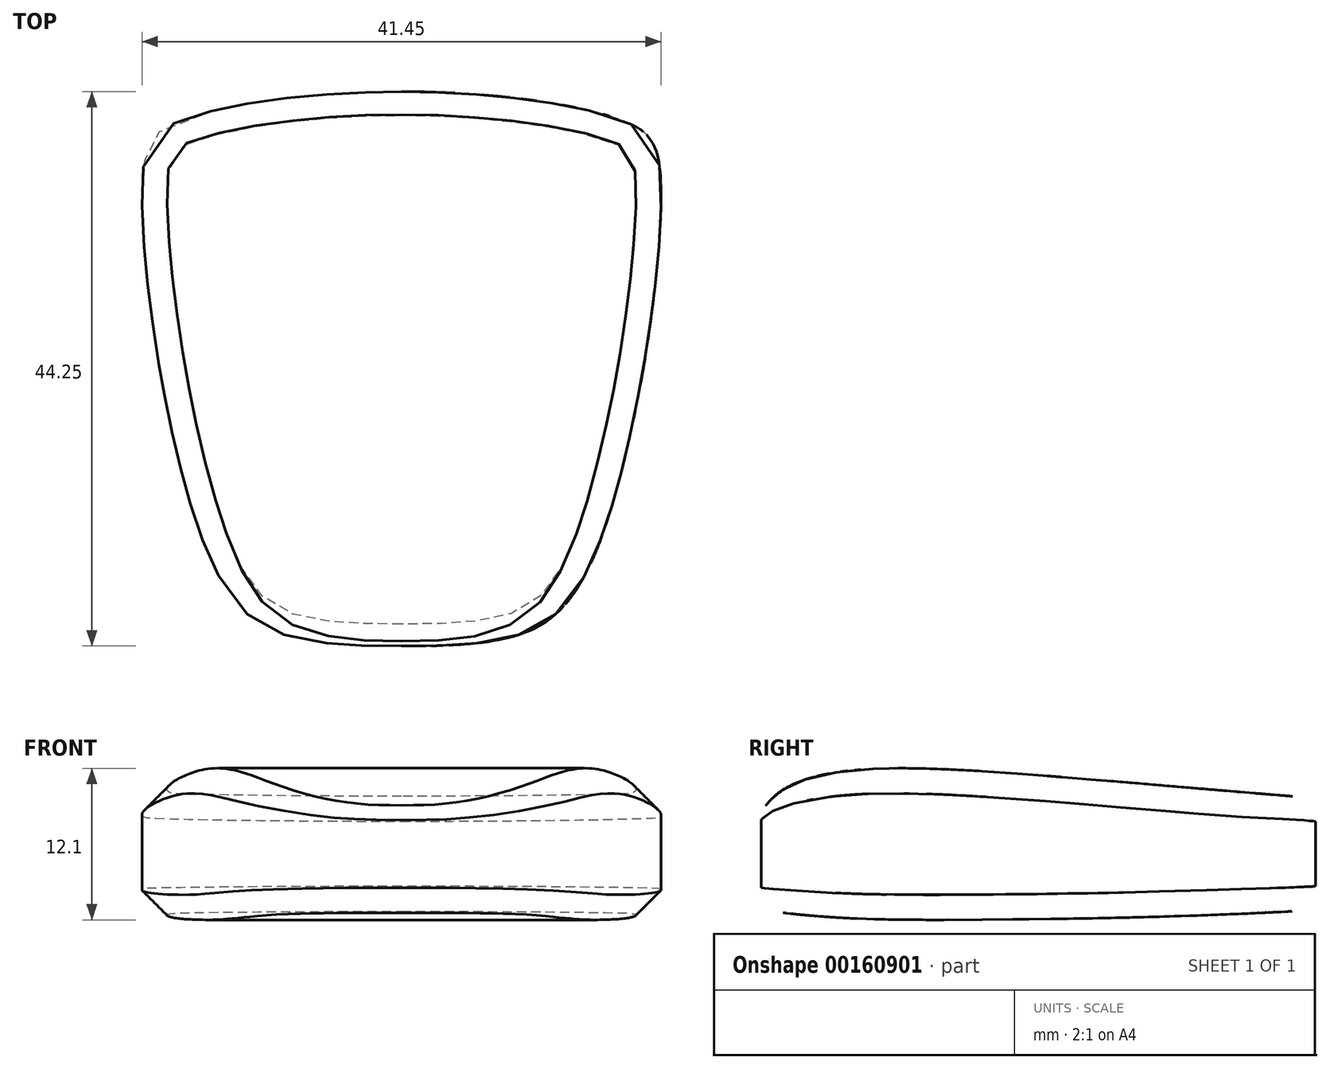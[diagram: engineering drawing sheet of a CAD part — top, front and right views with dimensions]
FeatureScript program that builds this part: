
annotation { "Feature Type Name" : "Feature", "Feature Type Description" : "" }
export const myFeature = defineFeature(function(context is Context, id is Id, definition is map)
    precondition{}
    {
        {
            var Q0;
            Q0=qCreatedBy(makeId("Top.planeOp"),FACE);
            var sketch = newSketch(context, id + "F0", { "sketchPlane" : qUnion([Q0])});
            skFitSpline(sketch, "E0", {"points": [v(0, 6.83) * mm, v(-18.05, 4.35) * mm, v(-20.68, 0) * mm, v(-15.04, -30.98) * mm, v(-8.66, -36.72) * mm, v(0, -37.42) * mm], "startDerivative": vector(-88.66, 0) * mm, "endDerivative": vector(58.86, 0) * mm});
            skFitSpline(sketch, "E1.MirrorCS", {"points": [v(0, 6.83) * mm, v(18.05, 4.35) * mm, v(20.68, 0) * mm, v(15.04, -30.98) * mm, v(8.66, -36.72) * mm, v(0, -37.42) * mm], "startDerivative": vector(88.66, 0) * mm, "endDerivative": vector(-58.86, 0) * mm});
            skSolve(sketch);
        }
        {
            var Q0;
            Q0 = qSketchRegion(id + "F0", true);
            extrude(context, id + "F1", {"entities" : qUnion([Q0]), "depth" : 13 * mm});
        }
        {
            var Q0;
            Q0=qCreatedBy(makeId("Right.planeOp"),FACE);
            var sketch = newSketch(context, id + "F2", { "sketchPlane" : qUnion([Q0])});
            skFitSpline(sketch, "E2", {"points": [v(8.15, 10) * mm, v(-16.67, 12.02) * mm, v(-33.98, 11.56) * mm, v(-37.82, 7.58) * mm], "startDerivative": vector(-56.28, 4.3) * mm, "endDerivative": vector(-4.26, -28.36) * mm});
            skLineSegment(sketch, "E3", {"start": v(8.15, 10) * mm, "end": v(9.66, 24.5) * mm});
            skLineSegment(sketch, "E4", {"start": v(9.66, 24.5) * mm, "end": v(-45.35, 17.25) * mm});
            skLineSegment(sketch, "E5", {"start": v(-45.35, 17.25) * mm, "end": v(-37.82, 7.58) * mm});
            skSolve(sketch);
        }
        {
            var Q0;
            Q0 = qSketchRegion(id + "F2", true);
            extrude(context, id + "F3", {"entities" : qUnion([Q0]), "operationType" : NewBodyOperationType.REMOVE, "endBound" : BoundingType.SYMMETRIC, "oppositeDirection" : true, "depth" : 50 * mm});
        }
        {
            var Q0;
            Q0=makeQuery(id+"F3.boolean.opBoolean","INTERSECT",EDGE,{"derivedFrom":[makeQuery(id+"F1.opExtrude","SWEPT_FACE",FACE,{"disambiguationData":[OSD([sQuery(id+"F0.wireOp",EDGE,"E0")])]}),makeQuery(id+"F3.opExtrude","SWEPT_FACE",FACE,{"disambiguationData":[OSD([sQuery(id+"F2.wireOp",EDGE,"E2")])]})]});
            chamfer(context, id + "F4", {"entities" : qUnion([Q0]), "width" : 2 * mm, "tangentPropagation" : true});
        }
        {
            var Q0;
            Q0=qCreatedBy(makeId("Right.planeOp"),FACE);
            var sketch = newSketch(context, id + "F5", { "sketchPlane" : qUnion([Q0])});
            skFitSpline(sketch, "E6", {"points": [v(7.54, 1.22) * mm, v(-20.49, 0.4) * mm, v(-41.97, 2.24) * mm, v(-49.82, 5.4) * mm, v(-49.95, 5.4) * mm], "startDerivative": vector(-67.16, -4.35) * mm, "endDerivative": vector(-3.18, -0.94) * mm});
            skLineSegment(sketch, "E7", {"start": v(7.54, 1.22) * mm, "end": v(14.63, -8.9) * mm});
            skLineSegment(sketch, "E8", {"start": v(14.63, -8.9) * mm, "end": v(-57.3, -6.5) * mm});
            skLineSegment(sketch, "E9", {"start": v(-57.3, -6.5) * mm, "end": v(-49.82, 5.4) * mm});
            skSolve(sketch);
        }
        {
            var Q0;
            Q0 = qSketchRegion(id + "F5", true);
            extrude(context, id + "F6", {"entities" : qUnion([Q0]), "operationType" : NewBodyOperationType.REMOVE, "endBound" : BoundingType.SYMMETRIC, "oppositeDirection" : true, "depth" : 50 * mm});
        }
        {
            var Q0;
            Q0=makeQuery(id+"F6.boolean.opBoolean","INTERSECT",EDGE,{"derivedFrom":[makeQuery(id+"F1.opExtrude","SWEPT_FACE",FACE,{"disambiguationData":[OSD([sQuery(id+"F0.wireOp",EDGE,"E0")])]}),makeQuery(id+"F6.opExtrude","SWEPT_FACE",FACE,{"disambiguationData":[OSD([sQuery(id+"F5.wireOp",EDGE,"E6")])]})]});
            chamfer(context, id + "F7", {"entities" : qUnion([Q0]), "width" : 2 * mm, "tangentPropagation" : true});
        }
    });
